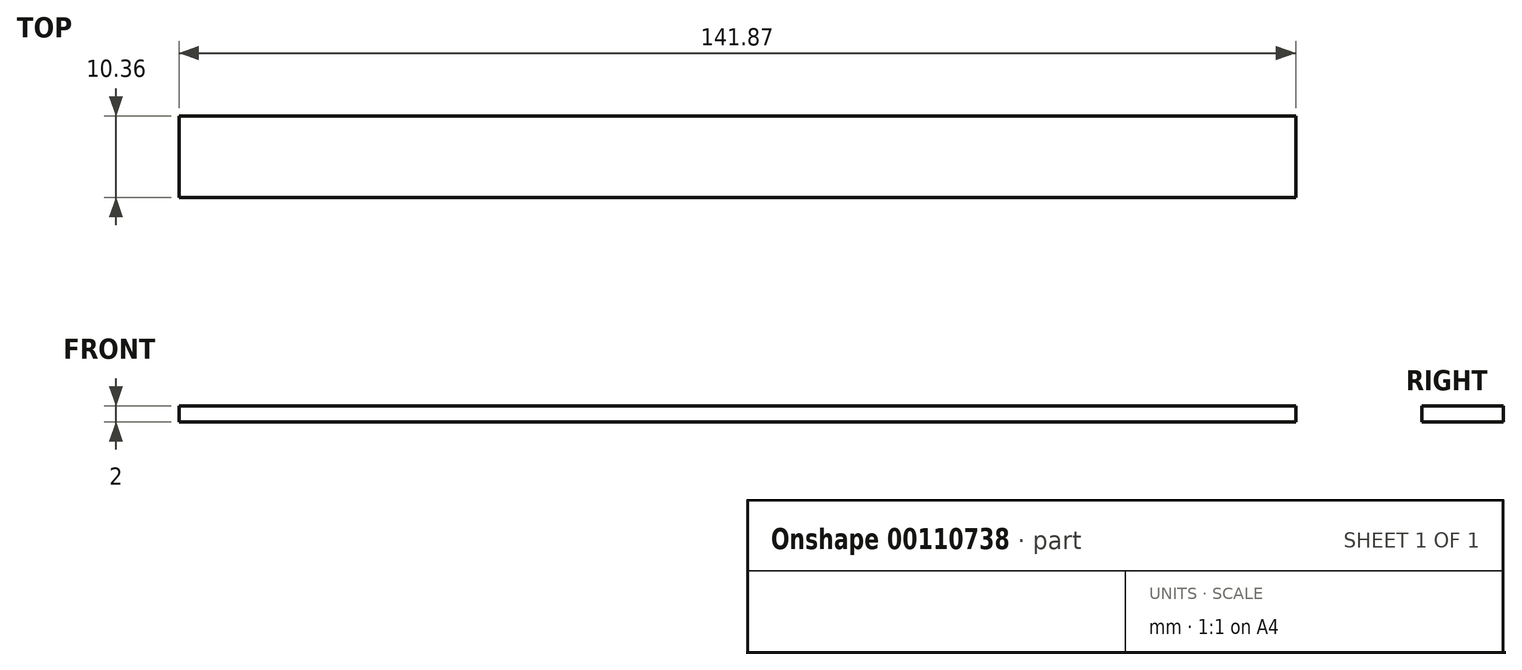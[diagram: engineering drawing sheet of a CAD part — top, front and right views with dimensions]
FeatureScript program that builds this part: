
annotation { "Feature Type Name" : "Feature", "Feature Type Description" : "" }
export const myFeature = defineFeature(function(context is Context, id is Id, definition is map)
    precondition{}
    {
        {
            var Q0;
            Q0=qCreatedBy(makeId("Top.planeOp"),FACE);
            var sketch = newSketch(context, id + "F0", { "sketchPlane" : qUnion([Q0])});
            skLineSegment(sketch, "E0.bottom", {"start": v(-71.72, 5.67) * mm, "end": v(70.15, 5.67) * mm});
            skLineSegment(sketch, "E0.top", {"start": v(-71.72, -4.69) * mm, "end": v(70.15, -4.69) * mm});
            skLineSegment(sketch, "E0.left", {"start": v(-71.72, 5.67) * mm, "end": v(-71.72, -4.69) * mm});
            skLineSegment(sketch, "E0.right", {"start": v(70.15, 5.67) * mm, "end": v(70.15, -4.69) * mm});
            skSolve(sketch);
        }
        {
            var Q0;
            Q0 = qSketchRegion(id + "F0", true);
            extrude(context, id + "F1", {"entities" : qUnion([Q0]), "depth" : 2 * mm});
        }
    });
